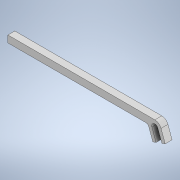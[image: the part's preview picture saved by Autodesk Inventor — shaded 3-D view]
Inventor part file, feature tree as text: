
AUTODESK INVENTOR PART (.ipt)
format: ipt  version: 2021 (Build 250183000, 183)  size: 142,848 bytes
history: native  units: mm
features: extrude x1, sketch x1
ambient origin geometry x8: Origin, YZ Plane, XZ Plane, XY Plane, X Axis, Y Axis, Z Axis, Center Point
bodies: Solid1 (feature_tree)
feature tree (2):
  extrude  "Extrusion1"  Depth=10.0mm
  sketch  "Sketch1"  dims[d31=20.0mm d32=0.0mm d38=10.0mm d39=10.0mm d40=9.0mm d47=20.0mm d53=9.0mm d56=400.0mm d58=200.0mm d59=35.0mm d60=3.490659mm d61=100.0mm]
